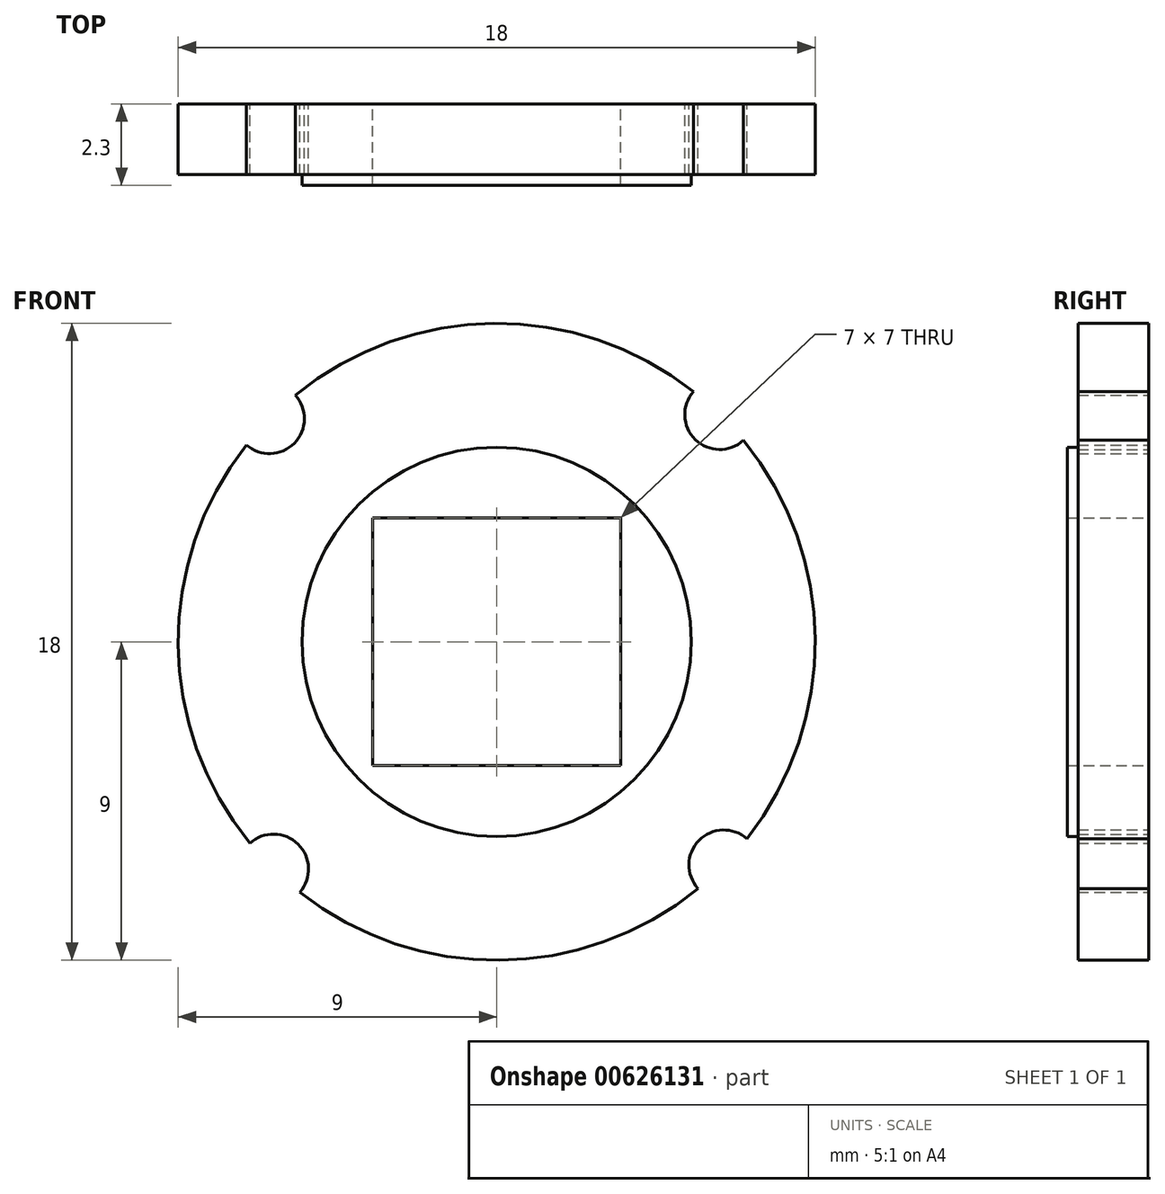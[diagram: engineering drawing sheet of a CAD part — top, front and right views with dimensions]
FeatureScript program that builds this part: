
annotation { "Feature Type Name" : "Feature", "Feature Type Description" : "" }
export const myFeature = defineFeature(function(context is Context, id is Id, definition is map)
    precondition{}
    {
        {
            var Q0;
            Q0=qCreatedBy(makeId("Front.planeOp"),FACE);
            var sketch = newSketch(context, id + "F0", { "sketchPlane" : qUnion([Q0])});
            skPoint(sketch, "E0.middle", {"position": v(0, 0) * mm});
            skArc(sketch, "E1", {"start": v(-7.07, 5.56) * mm, "mid": v(-9, -0.08) * mm, "end": v(-6.97, -5.7) * mm});
            skCircle(sketch, "E2", {"center": v(0, 0) * mm, "radius": 5.5 * mm});
            skPoint(sketch, "E0.bottom.start.orphan", {"position": v(-0.35, 0.35) * mm});
            skPoint(sketch, "E0.top.start.orphan", {"position": v(-0.35, -0.35) * mm});
            skPoint(sketch, "E0.right.end.orphan", {"position": v(0.35, -0.35) * mm});
            skPoint(sketch, "E0.right.start.orphan", {"position": v(0.35, 0.35) * mm});
            skLineSegment(sketch, "E3.bottom", {"start": v(-3.5, 3.5) * mm, "end": v(3.5, 3.5) * mm});
            skLineSegment(sketch, "E3.top", {"start": v(-3.5, -3.5) * mm, "end": v(3.5, -3.5) * mm});
            skLineSegment(sketch, "E3.left", {"start": v(-3.5, 3.5) * mm, "end": v(-3.5, -3.5) * mm});
            skLineSegment(sketch, "E3.right", {"start": v(3.5, 3.5) * mm, "end": v(3.5, -3.5) * mm});
            skArc(sketch, "E4", {"start": v(-7.07, 5.56) * mm, "mid": v(-5.72, 5.61) * mm, "end": v(-5.7, 6.97) * mm});
            skArc(sketch, "E5.1.0", {"start": v(-5.56, -7.07) * mm, "mid": v(-5.61, -5.72) * mm, "end": v(-6.97, -5.7) * mm});
            skArc(sketch, "E5.2.0", {"start": v(7.07, -5.56) * mm, "mid": v(5.72, -5.61) * mm, "end": v(5.7, -6.97) * mm});
            skArc(sketch, "E5.3.0", {"start": v(5.56, 7.07) * mm, "mid": v(5.61, 5.72) * mm, "end": v(6.97, 5.7) * mm});
            skArc(sketch, "E6.trimOffspring", {"start": v(5.56, 7.07) * mm, "mid": v(-0.08, 9) * mm, "end": v(-5.7, 6.97) * mm});
            skArc(sketch, "E7.trimOffspring", {"start": v(7.07, -5.56) * mm, "mid": v(9, 0.08) * mm, "end": v(6.97, 5.7) * mm});
            skArc(sketch, "E8.trimOffspring", {"start": v(-5.56, -7.07) * mm, "mid": v(0.08, -9) * mm, "end": v(5.7, -6.97) * mm});
            skSolve(sketch);
        }
        {
            var Q0;
            Q0=makeQuery(id+"F0.imprint","IMPRINT",FACE,{"disambiguationData":[TD([[makeQuery(id+"F0.imprint","IMPRINT",EDGE,{"derivedFrom":sQuery(id+"F0.wireOp",EDGE,"E1")}),1.0]])]});
            extrude(context, id + "F1", {"entities" : qUnion([Q0]), "depth" : 2 * mm, "offsetDistance" : 25 * mm});
        }
        {
            var Q0;
            Q0=makeQuery(id+"F0.imprint","IMPRINT",FACE,{"disambiguationData":[TD([[makeQuery(id+"F0.imprint","IMPRINT",EDGE,{"derivedFrom":sQuery(id+"F0.wireOp",EDGE,"E2")}),1.0]])]});
            extrude(context, id + "F2", {"entities" : qUnion([Q0]), "operationType" : NewBodyOperationType.ADD, "depth" : 2.3 * mm, "offsetDistance" : 25 * mm});
        }
    });
